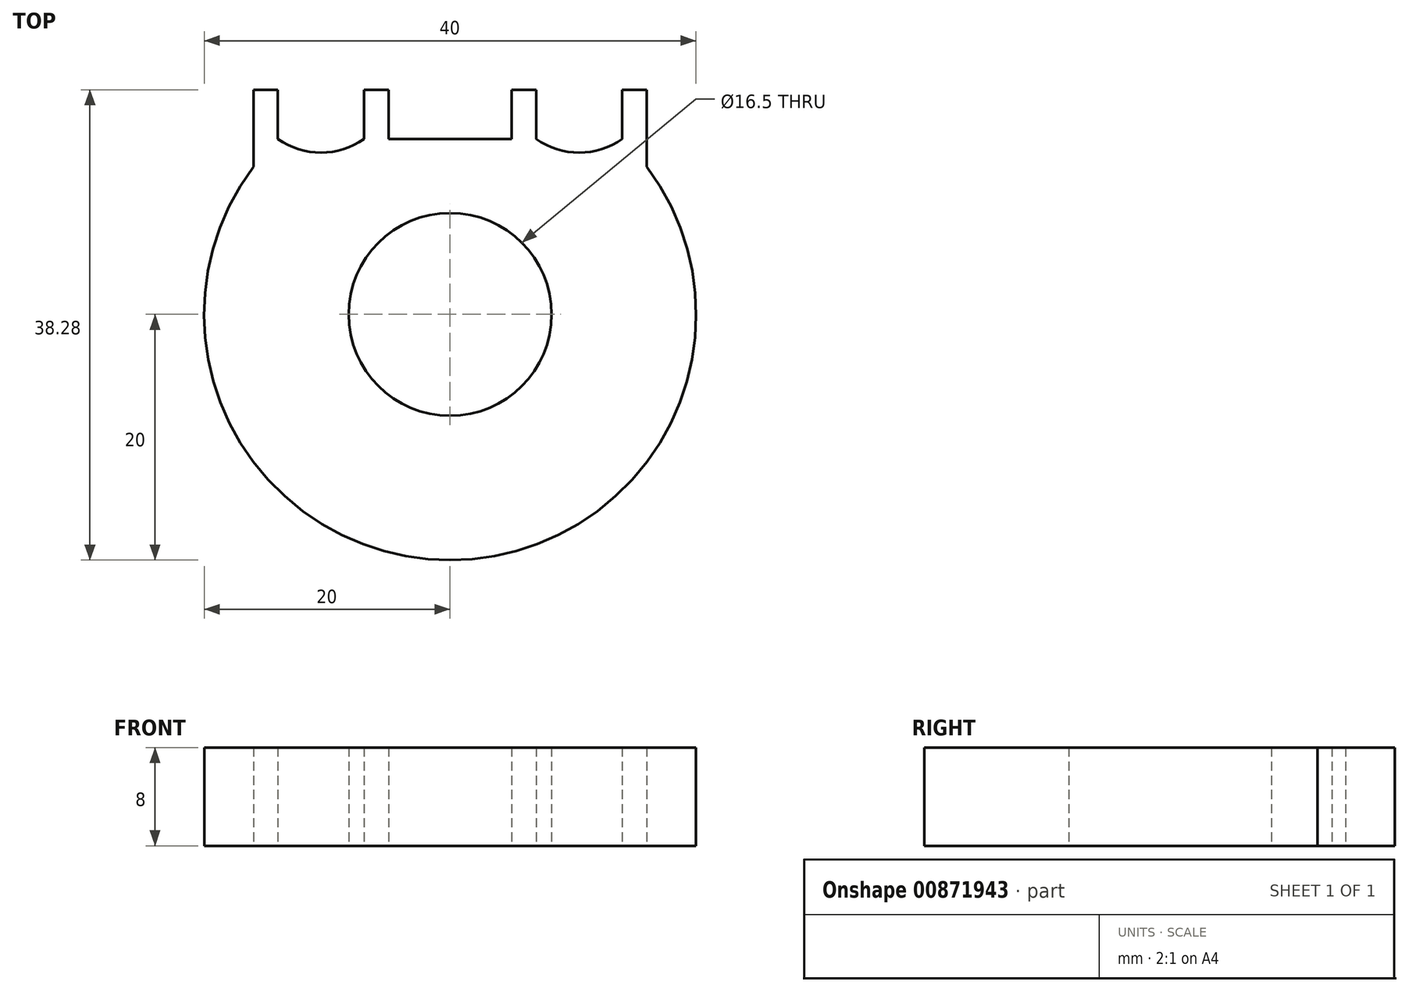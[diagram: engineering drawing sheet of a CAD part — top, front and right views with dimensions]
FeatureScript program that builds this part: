
annotation { "Feature Type Name" : "Feature", "Feature Type Description" : "" }
export const myFeature = defineFeature(function(context is Context, id is Id, definition is map)
    precondition{}
    {
        {
            var Q0;
            Q0=qCreatedBy(makeId("Top.planeOp"),FACE);
            var sketch = newSketch(context, id + "F0", { "sketchPlane" : qUnion([Q0])});
            skCircle(sketch, "E0", {"center": v(0, 0) * mm, "radius": 8.25 * mm});
            skArc(sketch, "E1", {"start": v(-16, 12) * mm, "mid": v(0, -20) * mm, "end": v(16, 12) * mm});
            skLineSegment(sketch, "E2", {"start": v(0, 24.78) * mm, "end": v(0, -25.08) * mm, "construction": true});
            skLineSegment(sketch, "E3", {"start": v(-23.27, 0) * mm, "end": v(25.77, 0) * mm, "construction": true});
            skLineSegment(sketch, "E4", {"start": v(-14, 14.28) * mm, "end": v(-14, 18.28) * mm});
            skLineSegment(sketch, "E5", {"start": v(-14, 18.28) * mm, "end": v(-16, 18.28) * mm});
            skLineSegment(sketch, "E6", {"start": v(-16, 18.28) * mm, "end": v(-16, 12) * mm});
            skLineSegment(sketch, "E7", {"start": v(-5, 14.28) * mm, "end": v(-5, 18.28) * mm});
            skLineSegment(sketch, "E8", {"start": v(-5, 18.28) * mm, "end": v(-7, 18.28) * mm});
            skLineSegment(sketch, "E9", {"start": v(-7, 18.28) * mm, "end": v(-7, 14.28) * mm});
            skLineSegment(sketch, "E10.MirrorCS", {"start": v(5, 14.28) * mm, "end": v(5, 18.28) * mm});
            skLineSegment(sketch, "E11.MirrorCS", {"start": v(5, 18.28) * mm, "end": v(7, 18.28) * mm});
            skLineSegment(sketch, "E12.MirrorCS", {"start": v(7, 18.28) * mm, "end": v(7, 14.28) * mm});
            skLineSegment(sketch, "E13.MirrorCS", {"start": v(14, 14.28) * mm, "end": v(14, 18.28) * mm});
            skLineSegment(sketch, "E14.MirrorCS", {"start": v(14, 18.28) * mm, "end": v(16, 18.28) * mm});
            skLineSegment(sketch, "E15.MirrorCS", {"start": v(16, 18.28) * mm, "end": v(16, 12) * mm});
            skLineSegment(sketch, "E16.trimOffspring", {"start": v(-5, 14.28) * mm, "end": v(0, 14.28) * mm});
            skLineSegment(sketch, "E17.trimOffspring", {"start": v(5, 14.28) * mm, "end": v(0, 14.28) * mm});
            skArc(sketch, "E18", {"start": v(-14, 14.28) * mm, "mid": v(-10.5, 13.16) * mm, "end": v(-7, 14.28) * mm});
            skArc(sketch, "E19.MirrorCS", {"start": v(14, 14.28) * mm, "mid": v(10.5, 13.16) * mm, "end": v(7, 14.28) * mm});
            skPoint(sketch, "E20.MirrorCS.start.orphan", {"position": v(14, 14.28) * mm});
            skSolve(sketch);
        }
        {
            var Q0;
            Q0=makeQuery(id+"F0.imprint","IMPRINT",FACE,{"disambiguationData":[TD([[makeQuery(id+"F0.imprint","IMPRINT",EDGE,{"derivedFrom":sQuery(id+"F0.wireOp",EDGE,"E0")}),-1.0]])]});
            extrude(context, id + "F1", {"entities" : qUnion([Q0]), "depth" : 8 * mm, "offsetDistance" : 25 * mm});
        }
    });
